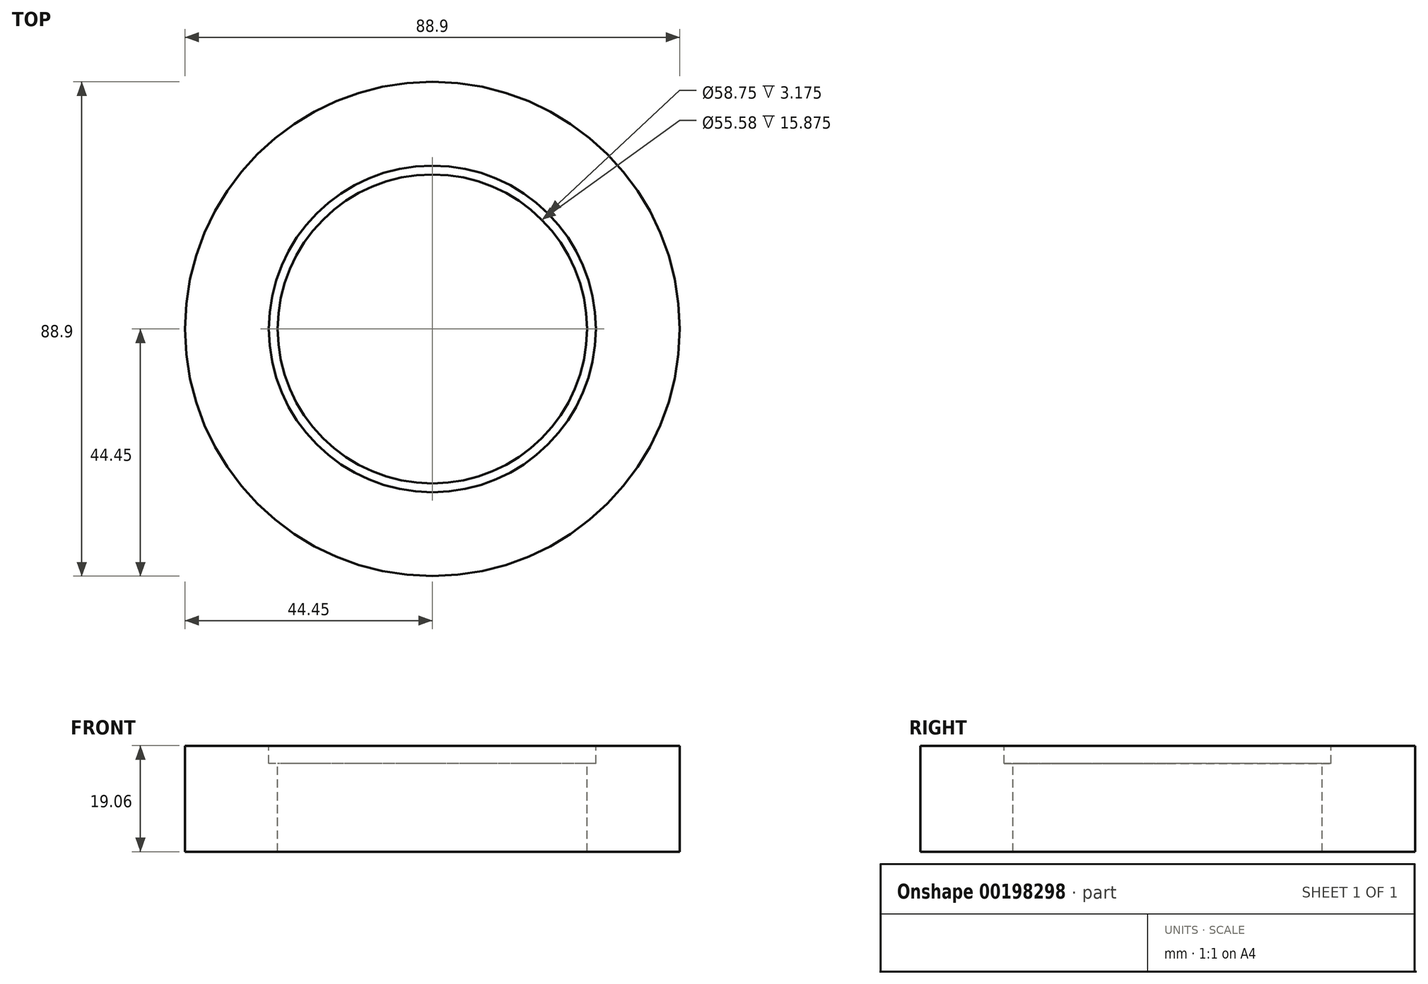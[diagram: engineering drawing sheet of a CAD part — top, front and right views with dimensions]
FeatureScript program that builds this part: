
annotation { "Feature Type Name" : "Feature", "Feature Type Description" : "" }
export const myFeature = defineFeature(function(context is Context, id is Id, definition is map)
    precondition{}
    {
        {
            var Q0;
            Q0=qCreatedBy(makeId("Top.planeOp"),FACE);
            var sketch = newSketch(context, id + "F0", { "sketchPlane" : qUnion([Q0])});
            skCircle(sketch, "E0", {"center": v(0, 0) * mm, "radius": 44.45 * mm});
            skSolve(sketch);
        }
        {
            var Q0;
            Q0=makeQuery(id+"F0.imprint","IMPRINT",FACE,{"disambiguationData":[TD([[makeQuery(id+"F0.imprint","IMPRINT",EDGE,{"derivedFrom":sQuery(id+"F0.wireOp",EDGE,"E0")}),1.0]])]});
            extrude(context, id + "F1", {"entities" : qUnion([Q0]), "endBound" : BoundingType.SYMMETRIC, "depth" : 19.05 * mm});
        }
        {
            var Q0;
            Q0=makeQuery(id+"F1.opExtrude","CAP_FACE",FACE,{"disambiguationData":[OSD([sQuery(id+"F0.wireOp",EDGE,"E0")])],"isStart":false});
            var sketch = newSketch(context, id + "F2", { "sketchPlane" : qUnion([Q0])});
            skCircle(sketch, "E1", {"center": v(0, 0) * mm, "radius": 29.38 * mm});
            skSolve(sketch);
        }
        {
            var Q0;
            Q0=makeQuery(id+"F2.imprint","IMPRINT",FACE,{"disambiguationData":[TD([[makeQuery(id+"F2.imprint","IMPRINT",EDGE,{"derivedFrom":sQuery(id+"F2.wireOp",EDGE,"E1")}),1.0]])]});
            extrude(context, id + "F3", {"entities" : qUnion([Q0]), "operationType" : NewBodyOperationType.REMOVE, "oppositeDirection" : true, "depth" : 3.17 * mm});
        }
        {
            var Q0;
            Q0=makeQuery(id+"F3.boolean.opBoolean","COPY",FACE,{"derivedFrom":makeQuery(id+"F3.opExtrude","CAP_FACE",FACE,{"disambiguationData":[OSD([sQuery(id+"F2.wireOp",EDGE,"E1")])],"isStart":false})});
            var sketch = newSketch(context, id + "F4", { "sketchPlane" : qUnion([Q0])});
            skCircle(sketch, "E2.0", {"center": v(0, 0) * mm, "radius": 27.79 * mm});
            skSolve(sketch);
        }
        {
            var Q0;
            Q0=makeQuery(id+"F4.imprint","IMPRINT",FACE,{"disambiguationData":[TD([[makeQuery(id+"F4.imprint","IMPRINT",EDGE,{"derivedFrom":sQuery(id+"F4.wireOp",EDGE,"E2.0")}),1.0]])]});
            extrude(context, id + "F5", {"entities" : qUnion([Q0]), "operationType" : NewBodyOperationType.REMOVE, "oppositeDirection" : true, "depth" : 15.88 * mm});
        }
    });
